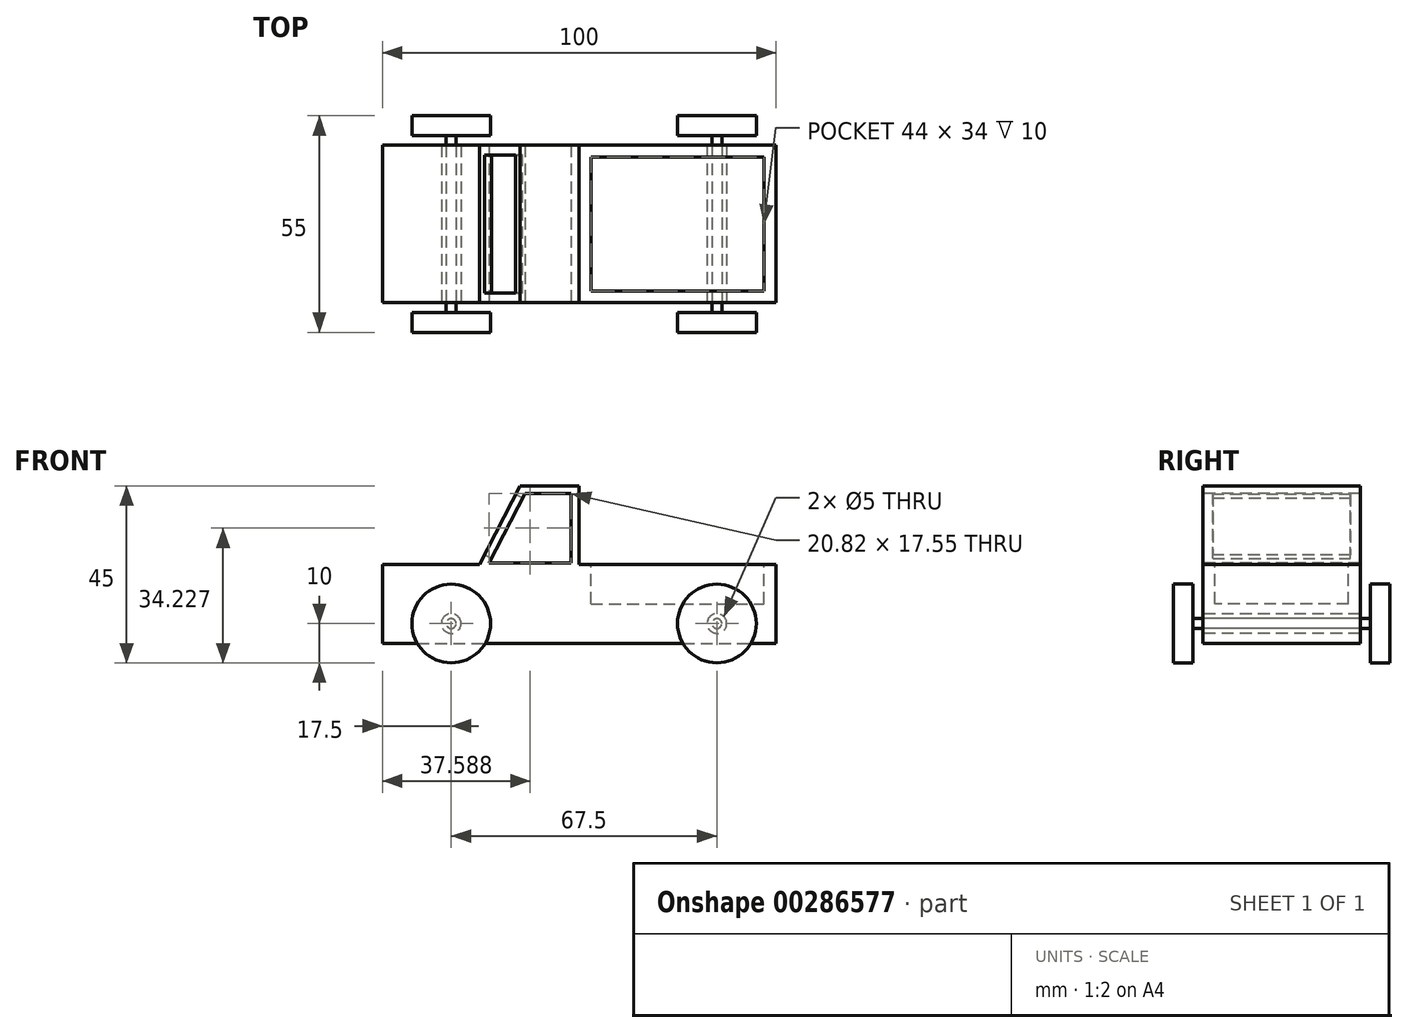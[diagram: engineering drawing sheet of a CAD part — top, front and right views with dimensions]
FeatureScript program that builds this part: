
annotation { "Feature Type Name" : "Feature", "Feature Type Description" : "" }
export const myFeature = defineFeature(function(context is Context, id is Id, definition is map)
    precondition{}
    {
        {
            var Q0;
            Q0=qCreatedBy(makeId("Front.planeOp"),FACE);
            var sketch = newSketch(context, id + "F0", { "sketchPlane" : qUnion([Q0])});
            skLineSegment(sketch, "E0.bottom", {"start": v(-50, 10) * mm, "end": v(50, 10) * mm});
            skLineSegment(sketch, "E0.top", {"start": v(-50, -10) * mm, "end": v(50, -10) * mm});
            skLineSegment(sketch, "E0.left", {"start": v(-50, 10) * mm, "end": v(-50, -10) * mm});
            skLineSegment(sketch, "E0.right", {"start": v(50, 10) * mm, "end": v(50, -10) * mm});
            skPoint(sketch, "E0.middle", {"position": v(0, 0) * mm});
            skPoint(sketch, "E1", {"position": v(0, 10) * mm});
            skLineSegment(sketch, "E2", {"start": v(0, 10) * mm, "end": v(0, 30) * mm});
            skLineSegment(sketch, "E3", {"start": v(0, 30) * mm, "end": v(-15, 30) * mm});
            skPoint(sketch, "E4", {"position": v(-25.3, 10) * mm});
            skLineSegment(sketch, "E5", {"start": v(-15, 30) * mm, "end": v(-25.3, 10) * mm});
            skCircle(sketch, "E6", {"center": v(-35, -5) * mm, "radius": 2.5 * mm});
            skCircle(sketch, "E7", {"center": v(35, -5) * mm, "radius": 2.5 * mm});
            skSolve(sketch);
        }
        {
            var Q0;
            Q0=makeQuery(id+"F0.imprint","IMPRINT",FACE,{"disambiguationData":[TD([[makeQuery(id+"F0.imprint","IMPRINT",EDGE,{"derivedFrom":sQuery(id+"F0.wireOp",EDGE,"E0.top")}),1.0]])]});
            var Q1;
            {var subQ0=sQuery(id+"F0.wireOp",EDGE,"E2");Q1=makeQuery(id+"F0.imprint","IMPRINT",FACE,{"disambiguationData":[TD([[makeQuery(id+"F0.imprint","IMPRINT",EDGE,{"derivedFrom":subQ0}),1.0]])]});}
            var Q2;
            Q2=makeQuery(id+"F0.imprint","IMPRINT",FACE,{"disambiguationData":[TD([[makeQuery(id+"F0.imprint","IMPRINT",EDGE,{"derivedFrom":sQuery(id+"F0.wireOp",EDGE,"E6")}),1.0]])]});
            var Q3;
            Q3=makeQuery(id+"F0.imprint","IMPRINT",FACE,{"disambiguationData":[TD([[makeQuery(id+"F0.imprint","IMPRINT",EDGE,{"derivedFrom":sQuery(id+"F0.wireOp",EDGE,"E7")}),1.0]])]});
            extrude(context, id + "F1", {"entities" : qUnion([Q0, Q1, Q2, Q3]), "endBound" : BoundingType.SYMMETRIC, "oppositeDirection" : true, "depth" : 40 * mm});
        }
        {
            var Q0;
            Q0=makeQuery(id+"F1.opExtrude","CAP_FACE",FACE,{"disambiguationData":[OSD([sQuery(id+"F0.wireOp",EDGE,"E0.bottom"),sQuery(id+"F0.wireOp",EDGE,"E0.top"),sQuery(id+"F0.wireOp",EDGE,"E0.left"),sQuery(id+"F0.wireOp",EDGE,"E0.right"),sQuery(id+"F0.wireOp",EDGE,"E2"),sQuery(id+"F0.wireOp",EDGE,"E3"),sQuery(id+"F0.wireOp",EDGE,"E5")])],"isStart":true});
            var sketch = newSketch(context, id + "F2", { "sketchPlane" : qUnion([Q0])});
            skCircle(sketch, "E8", {"center": v(-32.5, -5) * mm, "radius": 2.5 * mm});
            skCircle(sketch, "E9", {"center": v(35, -5) * mm, "radius": 2.5 * mm});
            skSolve(sketch);
        }
        {
            var Q0;
            Q0=makeQuery(id+"F2.imprint","IMPRINT",FACE,{"disambiguationData":[TD([[makeQuery(id+"F2.imprint","IMPRINT",EDGE,{"derivedFrom":sQuery(id+"F2.wireOp",EDGE,"E8")}),1.0]])]});
            var Q1;
            Q1=makeQuery(id+"F2.imprint","IMPRINT",FACE,{"disambiguationData":[TD([[makeQuery(id+"F2.imprint","IMPRINT",EDGE,{"derivedFrom":sQuery(id+"F2.wireOp",EDGE,"E9")}),1.0]])]});
            var Q2;
            Q2=sQuery(id+"F2.wireOp",EDGE,"E8");
            var Q3;
            Q3=sQuery(id+"F2.wireOp",EDGE,"E9");
            extrude(context, id + "F3", {"entities" : qUnion([Q0, Q1]), "operationType" : NewBodyOperationType.REMOVE, "surfaceEntities" : qUnion([Q2, Q3]), "endBound" : BoundingType.THROUGH_ALL, "oppositeDirection" : true, "depth" : 40 * mm});
        }
        {
            var Q0;
            {var subQ0=sQuery(id+"F0.wireOp",EDGE,"E0.bottom");Q0=makeQuery(id+"F1.opExtrude","SWEPT_FACE",FACE,{"disambiguationData":[OSD([subQ0]),TDD([makeQuery(id+"F0.imprint","IMPRINT",EDGE,{"disambiguationData":[TD([[makeQuery(id+"F0.imprint","INTERSECT",VERTEX,{"derivedFrom":[subQ0,sQuery(id+"F0.wireOp",EDGE,"E0.right")]}),1.0]])],"derivedFrom":subQ0})])]});}
            var sketch = newSketch(context, id + "F4", { "sketchPlane" : qUnion([Q0])});
            skLineSegment(sketch, "E10.bottom", {"start": v(3, 17) * mm, "end": v(47, 17) * mm});
            skLineSegment(sketch, "E10.top", {"start": v(3, -17) * mm, "end": v(47, -17) * mm});
            skLineSegment(sketch, "E10.left", {"start": v(3, 17) * mm, "end": v(3, -17) * mm});
            skLineSegment(sketch, "E10.right", {"start": v(47, 17) * mm, "end": v(47, -17) * mm});
            skSolve(sketch);
        }
        {
            var Q0;
            Q0=makeQuery(id+"F4.imprint","IMPRINT",FACE,{"disambiguationData":[TD([[makeQuery(id+"F4.imprint","IMPRINT",EDGE,{"derivedFrom":sQuery(id+"F4.wireOp",EDGE,"E10.bottom")}),-1.0]])]});
            extrude(context, id + "F5", {"entities" : qUnion([Q0]), "operationType" : NewBodyOperationType.REMOVE, "oppositeDirection" : true, "depth" : 10 * mm});
        }
        {
            var Q0;
            Q0=makeQuery(id+"F1.opExtrude","CAP_FACE",FACE,{"disambiguationData":[OSD([sQuery(id+"F0.wireOp",EDGE,"E0.bottom"),sQuery(id+"F0.wireOp",EDGE,"E0.top"),sQuery(id+"F0.wireOp",EDGE,"E0.left"),sQuery(id+"F0.wireOp",EDGE,"E0.right"),sQuery(id+"F0.wireOp",EDGE,"E2"),sQuery(id+"F0.wireOp",EDGE,"E3"),sQuery(id+"F0.wireOp",EDGE,"E5")])],"isStart":true});
            var sketch = newSketch(context, id + "F6", { "sketchPlane" : qUnion([Q0])});
            skCircle(sketch, "E11", {"center": v(35, -5) * mm, "radius": 1.25 * mm});
            skSolve(sketch);
        }
        {
            var Q0;
            Q0=makeQuery(id+"F6.imprint","IMPRINT",FACE,{"disambiguationData":[TD([[makeQuery(id+"F6.imprint","IMPRINT",EDGE,{"derivedFrom":sQuery(id+"F6.wireOp",EDGE,"E11")}),1.0]])]});
            var sketch = newSketch(context, id + "F7", { "sketchPlane" : qUnion([Q0])});
            skSolve(sketch);
        }
        {
            var Q0;
            Q0=makeQuery(id+"F6.imprint","IMPRINT",FACE,{"disambiguationData":[TD([[makeQuery(id+"F6.imprint","IMPRINT",EDGE,{"derivedFrom":sQuery(id+"F6.wireOp",EDGE,"E11")}),1.0]])]});
            var Q1;
            Q1=sQuery(id+"F6.wireOp",EDGE,"E11");
            extrude(context, id + "F8", {"entities" : qUnion([Q0]), "operationType" : NewBodyOperationType.ADD, "surfaceEntities" : qUnion([Q1]), "oppositeDirection" : true, "depth" : 42.5 * mm});
        }
        {
            var Q0;
            Q0=makeQuery(id+"F7.imprint","IMPRINT",FACE,{"disambiguationData":[TD([[makeQuery(id+"F7.imprint","IMPRINT",EDGE,{"derivedFrom":makeQuery(id+"F6.imprint","IMPRINT",EDGE,{"derivedFrom":sQuery(id+"F6.wireOp",EDGE,"E11")})}),1.0]])]});
            extrude(context, id + "F9", {"entities" : qUnion([Q0]), "operationType" : NewBodyOperationType.ADD, "depth" : 2.5 * mm});
        }
        {
            var Q0;
            Q0=makeQuery(id+"F1.opExtrude","CAP_FACE",FACE,{"disambiguationData":[OSD([sQuery(id+"F0.wireOp",EDGE,"E0.bottom"),sQuery(id+"F0.wireOp",EDGE,"E0.top"),sQuery(id+"F0.wireOp",EDGE,"E0.left"),sQuery(id+"F0.wireOp",EDGE,"E0.right"),sQuery(id+"F0.wireOp",EDGE,"E2"),sQuery(id+"F0.wireOp",EDGE,"E3"),sQuery(id+"F0.wireOp",EDGE,"E5")])],"isStart":true});
            var sketch = newSketch(context, id + "F10", { "sketchPlane" : qUnion([Q0])});
            skCircle(sketch, "E12", {"center": v(-32.5, -5) * mm, "radius": 1.25 * mm});
            skSolve(sketch);
        }
        {
            var Q0;
            Q0=makeQuery(id+"F10.imprint","IMPRINT",FACE,{"disambiguationData":[TD([[makeQuery(id+"F10.imprint","IMPRINT",EDGE,{"derivedFrom":sQuery(id+"F10.wireOp",EDGE,"E12")}),1.0]])]});
            extrude(context, id + "F11", {"entities" : qUnion([Q0]), "oppositeDirection" : true, "depth" : 42.5 * mm});
        }
        {
            var Q0;
            Q0=makeQuery(id+"F11.opExtrude","CAP_FACE",FACE,{"disambiguationData":[OSD([sQuery(id+"F10.wireOp",EDGE,"E12")])],"isStart":true});
            extrude(context, id + "F12", {"entities" : qUnion([Q0]), "operationType" : NewBodyOperationType.ADD, "depth" : 2.5 * mm});
        }
        {
            var Q0;
            Q0=makeQuery(id+"F12.opExtrude","CAP_FACE",FACE,{"disambiguationData":[OSD([sQuery(id+"F10.wireOp",EDGE,"E12")])],"isStart":false});
            var sketch = newSketch(context, id + "F13", { "sketchPlane" : qUnion([Q0])});
            skCircle(sketch, "E13", {"center": v(-32.5, -5) * mm, "radius": 10 * mm});
            skSolve(sketch);
        }
        {
            var Q0;
            Q0=makeQuery(id+"F9.opExtrude","CAP_FACE",FACE,{"disambiguationData":[OSD([sQuery(id+"F6.wireOp",EDGE,"E11")])],"isStart":false});
            var sketch = newSketch(context, id + "F14", { "sketchPlane" : qUnion([Q0])});
            skCircle(sketch, "E14", {"center": v(35, -5) * mm, "radius": 10 * mm});
            skSolve(sketch);
        }
        {
            var Q0;
            Q0=makeQuery(id+"F11.opExtrude","CAP_FACE",FACE,{"disambiguationData":[OSD([sQuery(id+"F10.wireOp",EDGE,"E12")])],"isStart":false});
            var sketch = newSketch(context, id + "F15", { "sketchPlane" : qUnion([Q0])});
            skCircle(sketch, "E15", {"center": v(32.5, -5) * mm, "radius": 10 * mm});
            skSolve(sketch);
        }
        {
            var Q0;
            Q0=makeQuery(id+"F8.opExtrude","CAP_FACE",FACE,{"disambiguationData":[OSD([sQuery(id+"F6.wireOp",EDGE,"E11")])],"isStart":false});
            var sketch = newSketch(context, id + "F16", { "sketchPlane" : qUnion([Q0])});
            skCircle(sketch, "E16", {"center": v(-35, -5) * mm, "radius": 10 * mm});
            skSolve(sketch);
        }
        {
            var Q0;
            Q0 = qSketchRegion(id + "F16", true);
            extrude(context, id + "F17", {"entities" : qUnion([Q0]), "operationType" : NewBodyOperationType.ADD, "depth" : 5 * mm});
        }
        {
            var Q0;
            Q0 = qSketchRegion(id + "F14", true);
            extrude(context, id + "F18", {"entities" : qUnion([Q0]), "operationType" : NewBodyOperationType.ADD, "depth" : 5 * mm});
        }
        {
            var Q0;
            Q0 = qSketchRegion(id + "F13", true);
            extrude(context, id + "F19", {"entities" : qUnion([Q0]), "operationType" : NewBodyOperationType.ADD, "depth" : 5 * mm});
        }
        {
            var Q0;
            Q0 = qSketchRegion(id + "F15", true);
            extrude(context, id + "F20", {"entities" : qUnion([Q0]), "operationType" : NewBodyOperationType.ADD, "depth" : 5 * mm});
        }
        {
            var Q0;
            Q0=makeQuery(id+"F1.opExtrude","SWEPT_FACE",FACE,{"disambiguationData":[OSD([sQuery(id+"F0.wireOp",EDGE,"E5")])]});
            var sketch = newSketch(context, id + "F21", { "sketchPlane" : qUnion([Q0])});
            skLineSegment(sketch, "E17.bottom", {"start": v(-17.5, 17.3) * mm, "end": v(17.5, 17.3) * mm});
            skLineSegment(sketch, "E17.top", {"start": v(-17.5, 0) * mm, "end": v(17.5, 0) * mm});
            skLineSegment(sketch, "E17.left", {"start": v(-17.5, 17.3) * mm, "end": v(-17.5, 0) * mm});
            skLineSegment(sketch, "E17.right", {"start": v(17.5, 17.3) * mm, "end": v(17.5, 0) * mm});
            skSolve(sketch);
        }
        {
            var Q0;
            Q0 = qSketchRegion(id + "F21", true);
            extrude(context, id + "F22", {"entities" : qUnion([Q0]), "operationType" : NewBodyOperationType.REMOVE, "oppositeDirection" : true, "depth" : 2.8 * mm});
        }
        {
            var Q0;
            Q0=makeQuery(id+"F1.opExtrude","CAP_FACE",FACE,{"disambiguationData":[OSD([sQuery(id+"F0.wireOp",EDGE,"E0.bottom"),sQuery(id+"F0.wireOp",EDGE,"E0.top"),sQuery(id+"F0.wireOp",EDGE,"E0.left"),sQuery(id+"F0.wireOp",EDGE,"E0.right"),sQuery(id+"F0.wireOp",EDGE,"E2"),sQuery(id+"F0.wireOp",EDGE,"E3"),sQuery(id+"F0.wireOp",EDGE,"E5")])],"isStart":true});
            var sketch = newSketch(context, id + "F23", { "sketchPlane" : qUnion([Q0])});
            skLineSegment(sketch, "E18.bottom", {"start": v(-2, 28) * mm, "end": v(-13.78, 28) * mm});
            skLineSegment(sketch, "E18.top", {"start": v(-2, 10.45) * mm, "end": v(-13.78, 10.45) * mm});
            skLineSegment(sketch, "E18.left", {"start": v(-2, 28) * mm, "end": v(-2, 10.45) * mm});
            skLineSegment(sketch, "E18.right", {"start": v(-13.78, 28) * mm, "end": v(-13.78, 10.45) * mm});
            skPoint(sketch, "E19", {"position": v(-22.82, 10.45) * mm});
            skLineSegment(sketch, "E20", {"start": v(-22.82, 10.45) * mm, "end": v(-13.78, 10.45) * mm});
            skLineSegment(sketch, "E21", {"start": v(-13.78, 28) * mm, "end": v(-22.82, 10.45) * mm});
            skSolve(sketch);
        }
        {
            var Q0;
            Q0=makeQuery(id+"F23.imprint","IMPRINT",FACE,{"disambiguationData":[TD([[makeQuery(id+"F23.imprint","IMPRINT",EDGE,{"derivedFrom":sQuery(id+"F23.wireOp",EDGE,"E18.right")}),-1.0]])]});
            var Q1;
            Q1=makeQuery(id+"F23.imprint","IMPRINT",FACE,{"disambiguationData":[TD([[makeQuery(id+"F23.imprint","IMPRINT",EDGE,{"derivedFrom":sQuery(id+"F23.wireOp",EDGE,"E18.bottom")}),1.0]])]});
            extrude(context, id + "F24", {"entities" : qUnion([Q0, Q1]), "operationType" : NewBodyOperationType.REMOVE, "oppositeDirection" : true, "depth" : 50.6 * mm});
        }
    });
